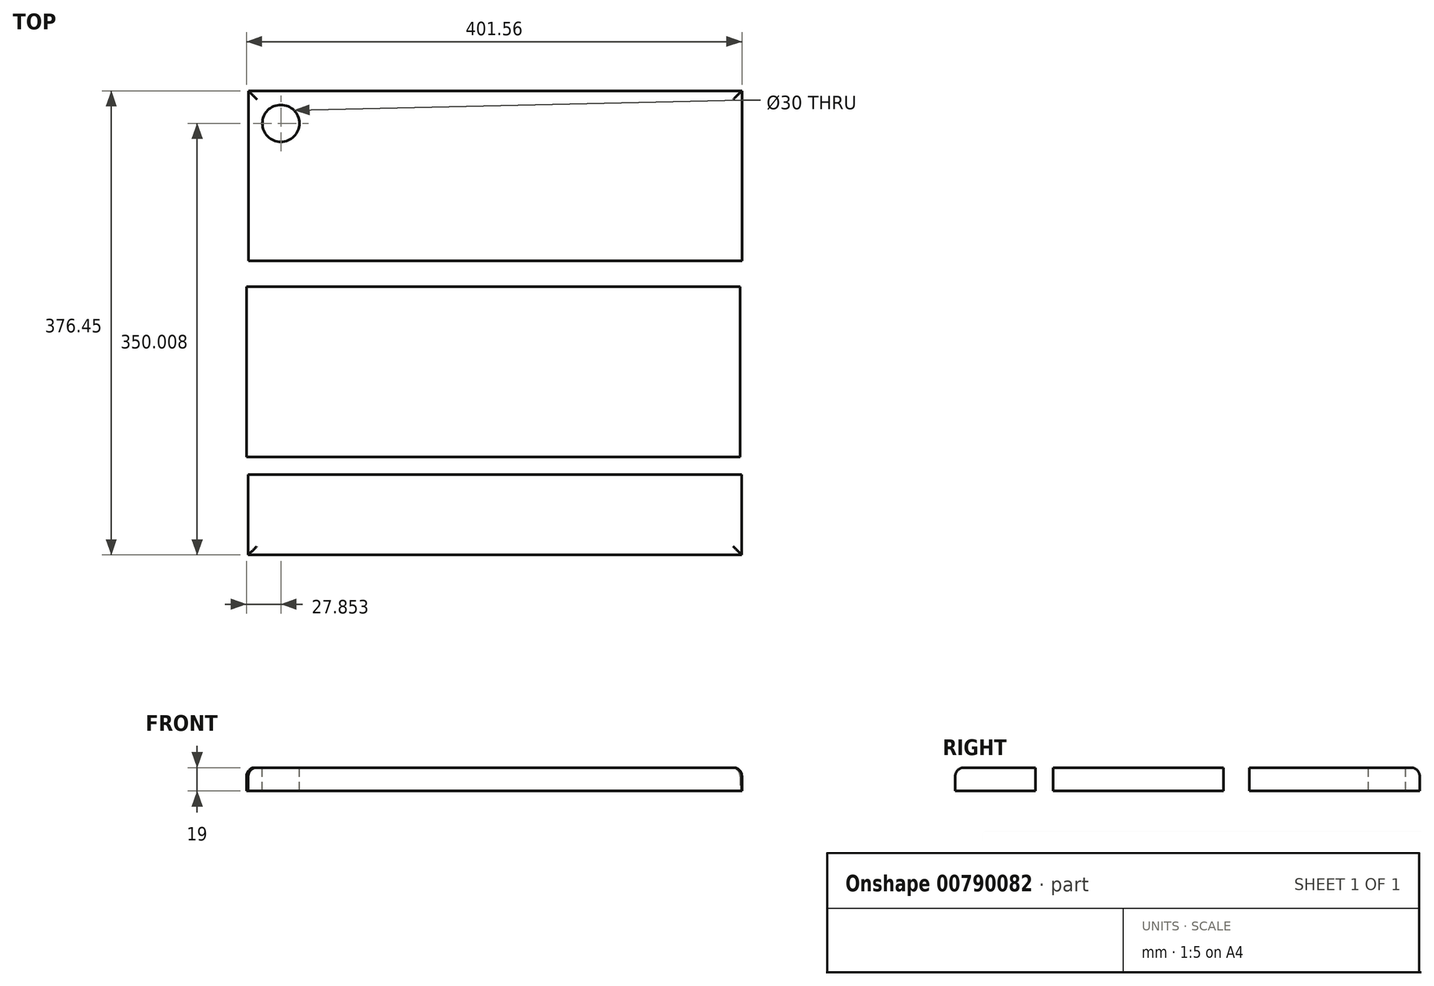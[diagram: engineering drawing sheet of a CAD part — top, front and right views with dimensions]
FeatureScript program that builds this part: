
annotation { "Feature Type Name" : "Feature", "Feature Type Description" : "" }
export const myFeature = defineFeature(function(context is Context, id is Id, definition is map)
    precondition{}
    {
        {
            var Q0;
            Q0=qCreatedBy(makeId("Top.planeOp"),FACE);
            var sketch = newSketch(context, id + "F0", { "sketchPlane" : qUnion([Q0])});
            skLineSegment(sketch, "E0.bottom", {"start": v(-277.46, 84.15) * mm, "end": v(122.54, 84.15) * mm});
            skLineSegment(sketch, "E0.top", {"start": v(-277.46, -53.85) * mm, "end": v(122.54, -53.85) * mm});
            skLineSegment(sketch, "E0.left", {"start": v(-277.46, 84.15) * mm, "end": v(-277.46, -53.85) * mm});
            skLineSegment(sketch, "E0.right", {"start": v(122.54, 84.15) * mm, "end": v(122.54, -53.85) * mm});
            skLineSegment(sketch, "E1.bottom", {"start": v(-276.04, -68.27) * mm, "end": v(123.96, -68.27) * mm});
            skLineSegment(sketch, "E1.top", {"start": v(-276.04, -133.27) * mm, "end": v(123.96, -133.27) * mm});
            skLineSegment(sketch, "E1.left", {"start": v(-276.04, -68.27) * mm, "end": v(-276.04, -133.27) * mm});
            skLineSegment(sketch, "E1.right", {"start": v(123.96, -68.27) * mm, "end": v(123.96, -133.27) * mm});
            skLineSegment(sketch, "E2.bottom", {"start": v(-275.9, 243.18) * mm, "end": v(124.1, 243.18) * mm});
            skLineSegment(sketch, "E2.top", {"start": v(-275.9, 105.18) * mm, "end": v(124.1, 105.18) * mm});
            skLineSegment(sketch, "E2.left", {"start": v(-275.9, 243.18) * mm, "end": v(-275.9, 105.18) * mm});
            skLineSegment(sketch, "E2.right", {"start": v(124.1, 243.18) * mm, "end": v(124.1, 105.18) * mm});
            skSolve(sketch);
        }
        {
            var Q0;
            Q0=makeQuery(id+"F0.imprint","IMPRINT",FACE,{"disambiguationData":[TD([[makeQuery(id+"F0.imprint","IMPRINT",EDGE,{"derivedFrom":sQuery(id+"F0.wireOp",EDGE,"E1.bottom")}),-1.0]])]});
            var Q1;
            Q1=makeQuery(id+"F0.imprint","IMPRINT",FACE,{"disambiguationData":[TD([[makeQuery(id+"F0.imprint","IMPRINT",EDGE,{"derivedFrom":sQuery(id+"F0.wireOp",EDGE,"E0.bottom")}),-1.0]])]});
            var Q2;
            Q2=makeQuery(id+"F0.imprint","IMPRINT",FACE,{"disambiguationData":[TD([[makeQuery(id+"F0.imprint","IMPRINT",EDGE,{"derivedFrom":sQuery(id+"F0.wireOp",EDGE,"E2.bottom")}),-1.0]])]});
            extrude(context, id + "F1", {"entities" : qUnion([Q0, Q1, Q2]), "depth" : 19 * mm, "offsetDistance" : 25 * mm});
        }
        {
            var Q0;
            Q0=makeQuery(id+"F1.opExtrude","CAP_EDGE",EDGE,{"disambiguationData":[OSD([sQuery(id+"F0.wireOp",EDGE,"E2.right")])],"isStart":false});
            var Q1;
            Q1=makeQuery(id+"F1.opExtrude","CAP_EDGE",EDGE,{"disambiguationData":[OSD([sQuery(id+"F0.wireOp",EDGE,"E2.bottom")])],"isStart":false});
            var Q2;
            Q2=makeQuery(id+"F1.opExtrude","CAP_EDGE",EDGE,{"disambiguationData":[OSD([sQuery(id+"F0.wireOp",EDGE,"E2.left")])],"isStart":false});
            var Q3;
            Q3=makeQuery(id+"F1.opExtrude","CAP_EDGE",EDGE,{"disambiguationData":[OSD([sQuery(id+"F0.wireOp",EDGE,"E0.right")])],"isStart":false});
            var Q4;
            Q4=makeQuery(id+"F1.opExtrude","CAP_EDGE",EDGE,{"disambiguationData":[OSD([sQuery(id+"F0.wireOp",EDGE,"E0.left")])],"isStart":false});
            var Q5;
            Q5=makeQuery(id+"F1.opExtrude","CAP_EDGE",EDGE,{"disambiguationData":[OSD([sQuery(id+"F0.wireOp",EDGE,"E1.left")])],"isStart":false});
            var Q6;
            Q6=makeQuery(id+"F1.opExtrude","CAP_EDGE",EDGE,{"disambiguationData":[OSD([sQuery(id+"F0.wireOp",EDGE,"E1.top")])],"isStart":false});
            var Q7;
            Q7=makeQuery(id+"F1.opExtrude","CAP_EDGE",EDGE,{"disambiguationData":[OSD([sQuery(id+"F0.wireOp",EDGE,"E1.right")])],"isStart":false});
            fillet(context, id + "F2", {"entities" : qUnion([Q0, Q1, Q2, Q3, Q4, Q5, Q6, Q7]), "radius" : 7 * mm, "tangentPropagation" : true, "allowEdgeOverflow" : false});
        }
        {
            var Q0;
            Q0=makeQuery(id+"F1.opExtrude","CAP_FACE",FACE,{"disambiguationData":[OSD([sQuery(id+"F0.wireOp",EDGE,"E2.bottom"),sQuery(id+"F0.wireOp",EDGE,"E2.top"),sQuery(id+"F0.wireOp",EDGE,"E2.left"),sQuery(id+"F0.wireOp",EDGE,"E2.right")])],"isStart":false});
            var sketch = newSketch(context, id + "F3", { "sketchPlane" : qUnion([Q0])});
            skCircle(sketch, "E3", {"center": v(-249.6, 216.74) * mm, "radius": 13.76 * mm});
            skSolve(sketch);
        }
        {
            var Q0;
            Q0=sQuery(id+"F3.wireOp",VERTEX,"E3.center");
            var Q1;
            Q1=makeQuery(id+"F1.opExtrude","SWEPT_BODY",BODY,{"disambiguationData":[OSD([sQuery(id+"F0.wireOp",EDGE,"E2.bottom"),sQuery(id+"F0.wireOp",EDGE,"E2.top"),sQuery(id+"F0.wireOp",EDGE,"E2.left"),sQuery(id+"F0.wireOp",EDGE,"E2.right")])]});
            hole(context, id + "F4", {"style" : HoleStyle.SIMPLE, "endStyle" : HoleEndStyle.THROUGH, "holeDiameter" : 30 * mm, "majorDiameter" : 5 * mm, "isTappedThrough" : true, "tappedDepth" : 12 * mm, "tapClearance" : 3, "locations" : qUnion([Q0]), "scope" : qUnion([Q1])});
        }
    });
